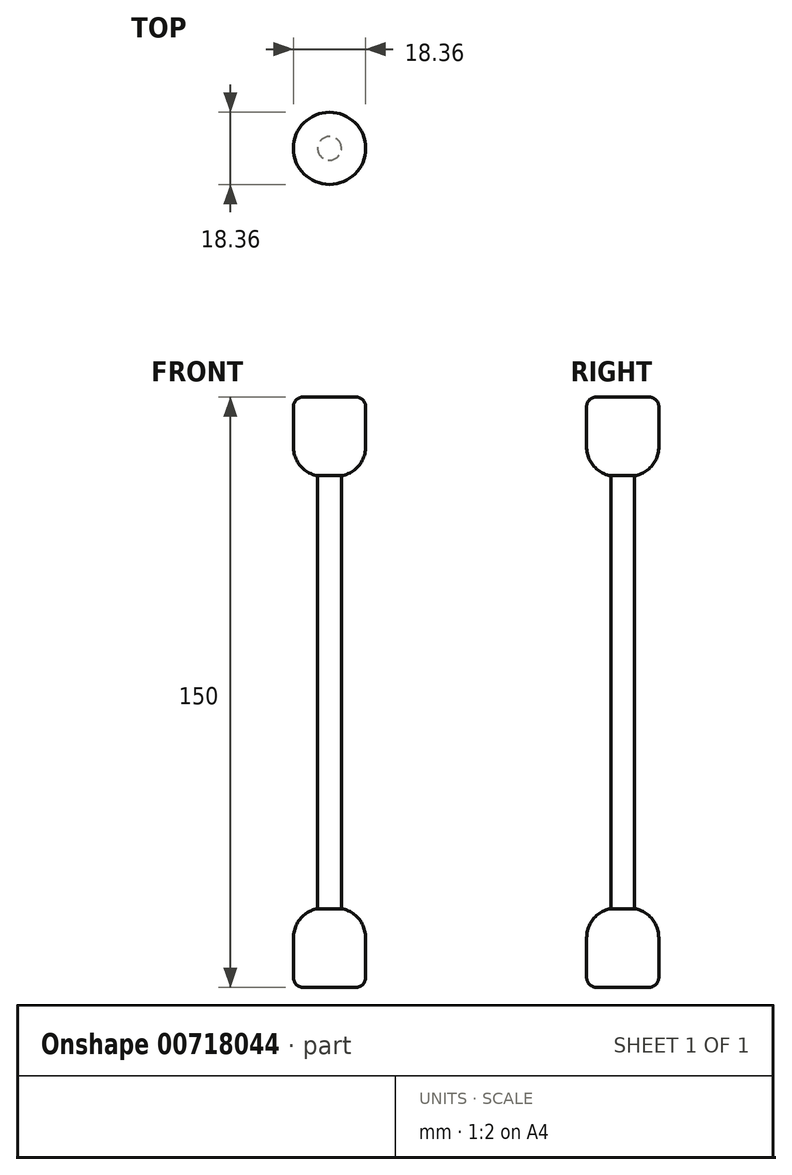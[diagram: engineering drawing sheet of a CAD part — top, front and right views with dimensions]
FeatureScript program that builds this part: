
annotation { "Feature Type Name" : "Feature", "Feature Type Description" : "" }
export const myFeature = defineFeature(function(context is Context, id is Id, definition is map)
    precondition{}
    {
        {
            var Q0;
            Q0=qCreatedBy(makeId("Top.planeOp"),FACE);
            var sketch = newSketch(context, id + "F0", { "sketchPlane" : qUnion([Q0])});
            skCircle(sketch, "E0", {"center": v(0, 0) * mm, "radius": 9.15 * mm});
            skSolve(sketch);
        }
        {
            var Q0;
            Q0 = qSketchRegion(id + "F0", true);
            extrude(context, id + "F1", {"entities" : qUnion([Q0]), "depth" : 20 * mm, "offsetDistance" : 25 * mm});
        }
        {
            var Q0;
            Q0=makeQuery(id+"F1.opExtrude","CAP_FACE",FACE,{"disambiguationData":[OSD([sQuery(id+"F0.wireOp",EDGE,"E0")])],"isStart":false});
            var sketch = newSketch(context, id + "F2", { "sketchPlane" : qUnion([Q0])});
            skCircle(sketch, "E1", {"center": v(0, 0) * mm, "radius": 3 * mm});
            skSolve(sketch);
        }
        {
            var Q0;
            Q0 = qSketchRegion(id + "F2", true);
            extrude(context, id + "F3", {"entities" : qUnion([Q0]), "operationType" : NewBodyOperationType.ADD, "depth" : 110 * mm, "offsetDistance" : 25 * mm});
        }
        {
            var Q0;
            Q0=makeQuery(id+"F3.opExtrude","CAP_FACE",FACE,{"disambiguationData":[OSD([sQuery(id+"F2.wireOp",EDGE,"E1")])],"isStart":false});
            var sketch = newSketch(context, id + "F4", { "sketchPlane" : qUnion([Q0])});
            skCircle(sketch, "E2", {"center": v(0, 0) * mm, "radius": 9.18 * mm});
            skSolve(sketch);
        }
        {
            var Q0;
            Q0 = qSketchRegion(id + "F4", true);
            extrude(context, id + "F5", {"entities" : qUnion([Q0]), "operationType" : NewBodyOperationType.ADD, "depth" : 20 * mm, "offsetDistance" : 25 * mm});
        }
        {
            var Q0;
            Q0=makeQuery(id+"F1.opExtrude","CAP_EDGE",EDGE,{"disambiguationData":[OSD([sQuery(id+"F0.wireOp",EDGE,"E0")])],"isStart":false});
            var Q1;
            Q1=makeQuery(id+"F5.opExtrude","CAP_EDGE",EDGE,{"disambiguationData":[OSD([sQuery(id+"F4.wireOp",EDGE,"E2")])],"isStart":true});
            fillet(context, id + "F6", {"entities" : qUnion([Q0, Q1]), "radius" : 7.5 * mm, "tangentPropagation" : true, "allowEdgeOverflow" : false});
        }
        {
            var Q0;
            Q0=makeQuery(id+"F5.opExtrude","CAP_EDGE",EDGE,{"disambiguationData":[OSD([sQuery(id+"F4.wireOp",EDGE,"E2")])],"isStart":false});
            var Q1;
            Q1=makeQuery(id+"F1.opExtrude","CAP_EDGE",EDGE,{"disambiguationData":[OSD([sQuery(id+"F0.wireOp",EDGE,"E0")])],"isStart":true});
            fillet(context, id + "F7", {"entities" : qUnion([Q0, Q1]), "radius" : 2.5 * mm, "tangentPropagation" : true, "allowEdgeOverflow" : false});
        }
    });
